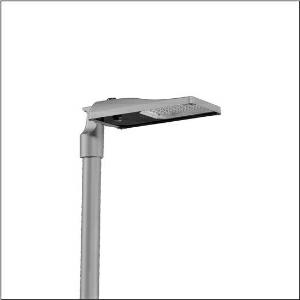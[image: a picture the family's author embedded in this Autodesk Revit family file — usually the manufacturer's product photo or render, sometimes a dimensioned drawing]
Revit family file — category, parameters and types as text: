
# Revit family: streetlight_sl_31_mini___st1_0a_5xh6d3at08ha_0bc3
name_source: partatom
category: Lighting Fixtures
units: mm (PartAtom-declared; Revit-internal decimal feet)

## family parameters
Cut with Voids When Loaded = No
Host = Face
Light Source = No
Part Type = Normal
Room Calculation Point = No
Round Connector Dimension = Use Diameter
Shared = No

## types (1)
- --- (1 x LED, 9230 lm, 68.3 W, 3000K)
    Apparent Load = 68 VA
    CIE Flux Codes = 37 72 97 100 100
    Color Rendering = 70
    Color Temperature = 3000K
    Default Elevation = 1800 mm
    Description = Streetlight SL 31 mini D4i mast luminaire for post-top, side-entry; light control with lens of PMMA; light distribution: ST1.0a, direct asymmetric distribution, for standard-compliant lighting for roads and squares; LED: luminous flux: 9.230lm, light colour: 730, colour temperature: 3000K; luminous efficacy: 135,1lm/W; control: pre-setting: logarithmic dimming characteristic, flexible luminous flux parameterisation, time-dependent luminous flux control, constant luminous flux control, power reduction, intelligent temperature release in ECG and LED module, overheat protection; luminaire housing, of diecast aluminium, Siteco® metallic grey (DB 702S), corrosivity category C5 high according to DIN EN ISO 12944; cover of toughened safety glass, transparent, opened without tools; mast flange of diecast aluminium, Siteco® metallic grey (DB 702S), spigot size: 76/60mm, mast flange included unmounted; with cable H07RN-F 2x 1.5mm², cable length: 8,5m, connection cable pre-assembled; mains connection: 220..240V, AC, 50/60Hz; power consumption (at start of service life): 68,3W / (at end of service life): 74,5W / (with reduced operation 50%): 29,5W; protection rating (complete): IP66; insulation class (complete): insulation class II (safety insulation); impact resistance: IK09; certification: CE, ENEC, ENEC+, VDE, UKCA, ZD4i; permissible operating ambient temperature for outdoor applications: -40..+50°C; packaging unit: 1 piece

Light Distribution: ST1.0a
    Height = 76 mm
    Lamp = 1 x LED
    Lamp Light Flux = 9230 lm
    Lamp Power = 68.3 W
    Lamp count = 1
    Length = 547 mm
    Luminous efficacy = 135 lm/W
    Manufacturer = Siteco
    ModVariant = No
    Model = 5XH6D3AT08HA
    Number of Poles = 1
    OnlyDefault = Yes
    Power Factor = 1
    Product Name = Streetlight SL 31 mini | ST1.0a
    Product group = mast luminaire | pylon top
    ProductGroupID = 6100
    Protection Class = Protection class II
    Protection Degree = IP 66
    RLX_Detail_Level = 1
    RLX_Emergency_Light_Flux = 0 lm
    RLX_Emergency_Type = 0
    RLX_Emergency_Type_DB = No
    RlxData = <blob elided: 24337 chars, md5=060644f3>
    Socket = socket
    Standby Power = 0 W
    System Light Flux = 9230 lm
    System Power = 68 W
    Type Comments = factory setting: luminous flux: 100 % | dim-lin: 254 | 692 mA
    Type Image = l_1300332.jpg
    URL = http://relux.com
    VarID = @adj_001831
    Voltage = 0 V
    Weight = 0.00 kg
    Width = 265 mm

## geometry (parser evidence)
native form markers: Blend x4, Sweep x11
no freeform markers — native parametric forms only
